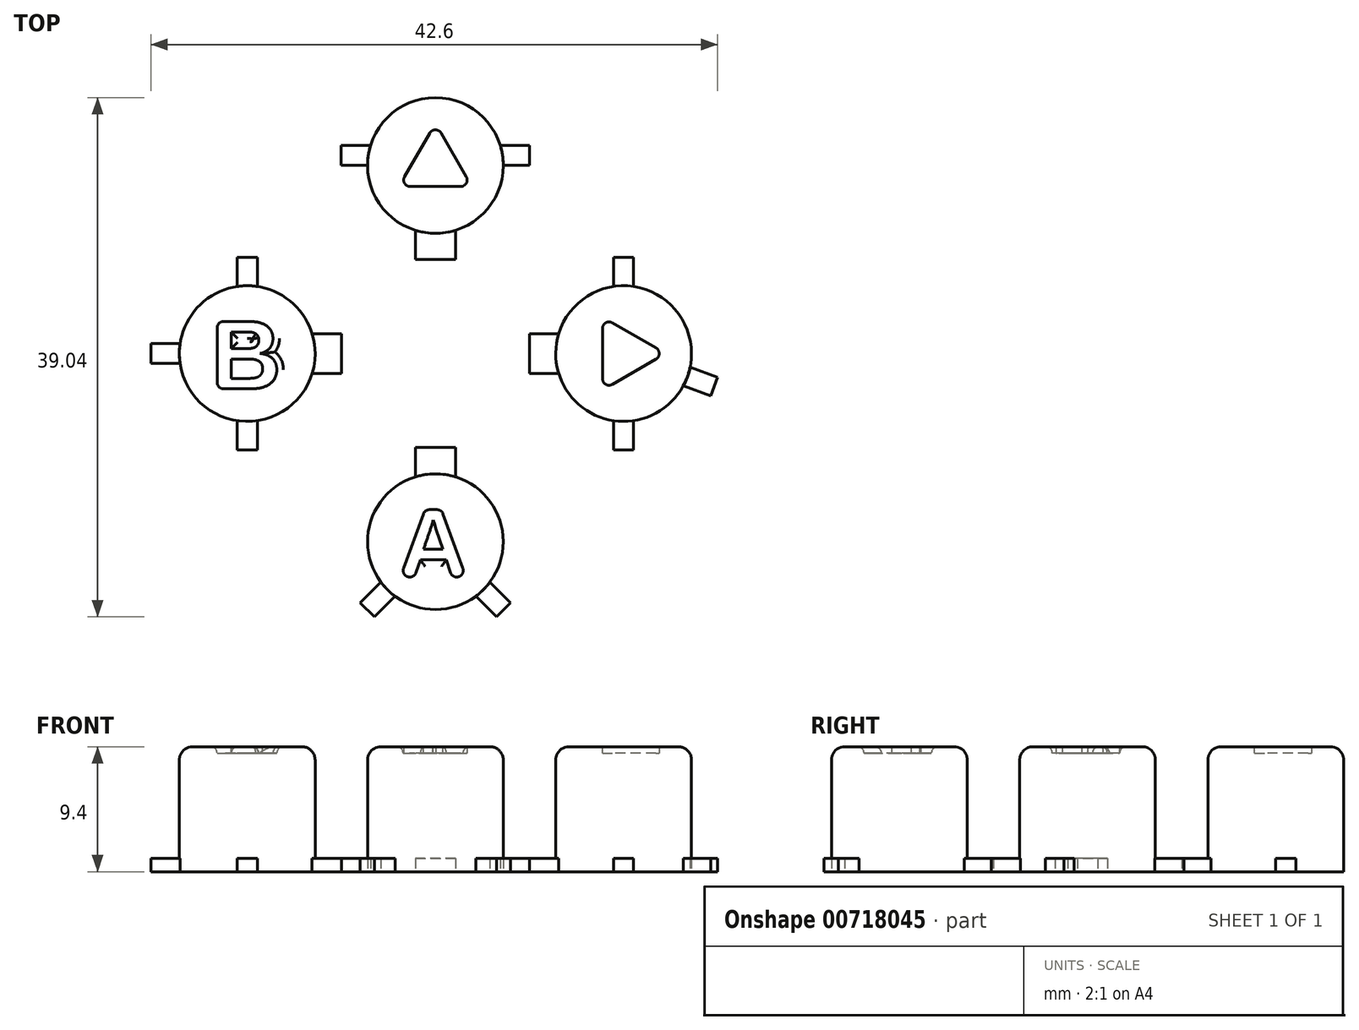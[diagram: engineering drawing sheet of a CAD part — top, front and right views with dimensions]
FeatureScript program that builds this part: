
annotation { "Feature Type Name" : "Feature", "Feature Type Description" : "" }
export const myFeature = defineFeature(function(context is Context, id is Id, definition is map)
    precondition{}
    {
        {
            var Q0;
            Q0=qCreatedBy(makeId("Top.planeOp"),FACE);
            var sketch = newSketch(context, id + "F0", { "sketchPlane" : qUnion([Q0])});
            skCircle(sketch, "E0", {"center": v(0, 14.14) * mm, "radius": 5.1 * mm});
            skLineSegment(sketch, "E1.top", {"start": v(1.5, 7.07) * mm, "end": v(-1.5, 7.07) * mm});
            skLineSegment(sketch, "E1.left", {"start": v(1.5, 9.27) * mm, "end": v(1.5, 7.07) * mm});
            skLineSegment(sketch, "E1.right", {"start": v(-1.5, 9.27) * mm, "end": v(-1.5, 7.07) * mm});
            skLineSegment(sketch, "E2.bottom", {"start": v(-7.07, 15.64) * mm, "end": v(-4.87, 15.64) * mm});
            skLineSegment(sketch, "E2.top", {"start": v(-7.07, 14.14) * mm, "end": v(-5.1, 14.14) * mm});
            skLineSegment(sketch, "E2.left", {"start": v(-7.07, 15.64) * mm, "end": v(-7.07, 14.14) * mm});
            skLineSegment(sketch, "E2.right", {"start": v(7.07, 15.64) * mm, "end": v(7.07, 14.14) * mm});
            skLineSegment(sketch, "E3.trimOffspring", {"start": v(4.87, 15.64) * mm, "end": v(7.07, 15.64) * mm});
            skLineSegment(sketch, "E4.trimOffspring", {"start": v(5.1, 14.14) * mm, "end": v(7.07, 14.14) * mm});
            skLineSegment(sketch, "E5.bottom", {"start": v(-14.14, 0) * mm, "end": v(0, 14.14) * mm, "construction": true});
            skLineSegment(sketch, "E5.top", {"start": v(0, -14.14) * mm, "end": v(14.14, 0) * mm, "construction": true});
            skLineSegment(sketch, "E5.left", {"start": v(-14.14, 0) * mm, "end": v(0, -14.14) * mm, "construction": true});
            skLineSegment(sketch, "E5.right", {"start": v(0, 14.14) * mm, "end": v(14.14, 0) * mm, "construction": true});
            skPoint(sketch, "E5.middle", {"position": v(0, 0) * mm});
            skCircle(sketch, "E6", {"center": v(14.14, 0) * mm, "radius": 5.1 * mm});
            skCircle(sketch, "E7", {"center": v(0, -14.14) * mm, "radius": 5.1 * mm});
            skLineSegment(sketch, "E8", {"start": v(0, 14.14) * mm, "end": v(0, 0) * mm, "construction": true});
            skLineSegment(sketch, "E9.bottom", {"start": v(-1.5, -7.07) * mm, "end": v(1.5, -7.07) * mm});
            skLineSegment(sketch, "E9.left", {"start": v(-1.5, -7.07) * mm, "end": v(-1.5, -9.27) * mm});
            skLineSegment(sketch, "E9.right", {"start": v(1.5, -7.07) * mm, "end": v(1.5, -9.27) * mm});
            skLineSegment(sketch, "E10.bottom", {"start": v(7.07, 1.5) * mm, "end": v(9.27, 1.5) * mm});
            skLineSegment(sketch, "E10.top", {"start": v(7.07, -1.5) * mm, "end": v(9.27, -1.5) * mm});
            skLineSegment(sketch, "E10.left", {"start": v(7.07, 1.5) * mm, "end": v(7.07, -1.5) * mm});
            skLineSegment(sketch, "E11", {"start": v(13.4, 5.04) * mm, "end": v(13.4, 7.24) * mm});
            skLineSegment(sketch, "E12", {"start": v(13.4, 7.24) * mm, "end": v(14.9, 7.24) * mm});
            skLineSegment(sketch, "E13", {"start": v(14.9, 7.24) * mm, "end": v(14.9, 5.04) * mm});
            skLineSegment(sketch, "E14", {"start": v(13.4, -5.04) * mm, "end": v(13.4, -7.24) * mm});
            skLineSegment(sketch, "E15", {"start": v(13.4, -7.24) * mm, "end": v(14.9, -7.24) * mm});
            skLineSegment(sketch, "E16", {"start": v(14.9, -7.24) * mm, "end": v(14.9, -5.04) * mm});
            skLineSegment(sketch, "E17.top", {"start": v(20.7, -3.18) * mm, "end": v(21.2, -1.77) * mm});
            skLineSegment(sketch, "E17.left", {"start": v(18.63, -2.43) * mm, "end": v(20.7, -3.18) * mm});
            skLineSegment(sketch, "E17.right", {"start": v(19.14, -1.02) * mm, "end": v(21.2, -1.77) * mm});
            skLineSegment(sketch, "E18", {"start": v(14.14, 0) * mm, "end": v(20.95, -2.48) * mm, "construction": true});
            skCircle(sketch, "E19", {"center": v(-14.14, 0) * mm, "radius": 5.1 * mm});
            skLineSegment(sketch, "E20.bottom", {"start": v(-9.27, 1.5) * mm, "end": v(-7.07, 1.5) * mm});
            skLineSegment(sketch, "E20.top", {"start": v(-9.27, -1.5) * mm, "end": v(-7.07, -1.5) * mm});
            skLineSegment(sketch, "E20.right", {"start": v(-7.07, 1.5) * mm, "end": v(-7.07, -1.5) * mm});
            skLineSegment(sketch, "E21.bottom", {"start": v(-14.9, 7.24) * mm, "end": v(-13.4, 7.24) * mm});
            skLineSegment(sketch, "E21.top", {"start": v(-14.9, -7.24) * mm, "end": v(-13.4, -7.24) * mm});
            skLineSegment(sketch, "E21.left", {"start": v(-14.9, 7.24) * mm, "end": v(-14.9, 5.04) * mm});
            skLineSegment(sketch, "E21.right", {"start": v(-13.4, 7.24) * mm, "end": v(-13.4, 5.04) * mm});
            skLineSegment(sketch, "E22.bottom", {"start": v(-21.39, 0.75) * mm, "end": v(-19.19, 0.75) * mm});
            skLineSegment(sketch, "E22.top", {"start": v(-21.39, -0.75) * mm, "end": v(-19.19, -0.75) * mm});
            skLineSegment(sketch, "E22.left", {"start": v(-21.39, 0.75) * mm, "end": v(-21.39, -0.75) * mm});
            skLineSegment(sketch, "E23.trimOffspring", {"start": v(-14.9, -5.04) * mm, "end": v(-14.9, -7.24) * mm});
            skLineSegment(sketch, "E24.trimOffspring", {"start": v(-13.4, -5.04) * mm, "end": v(-13.4, -7.24) * mm});
            skLineSegment(sketch, "E25", {"start": v(0, -14.14) * mm, "end": v(5.12, -19.26) * mm, "construction": true});
            skLineSegment(sketch, "E26", {"start": v(0, -14.14) * mm, "end": v(-5.12, -19.26) * mm, "construction": true});
            skLineSegment(sketch, "E27.top", {"start": v(-5.65, -18.73) * mm, "end": v(-4.6, -19.8) * mm});
            skLineSegment(sketch, "E27.left", {"start": v(-4.1, -17.18) * mm, "end": v(-5.65, -18.73) * mm});
            skLineSegment(sketch, "E27.right", {"start": v(-3.04, -18.24) * mm, "end": v(-4.6, -19.8) * mm});
            skLineSegment(sketch, "E28", {"start": v(3.04, -18.24) * mm, "end": v(4.6, -19.8) * mm});
            skLineSegment(sketch, "E29", {"start": v(4.6, -19.8) * mm, "end": v(5.65, -18.73) * mm});
            skLineSegment(sketch, "E30", {"start": v(5.65, -18.73) * mm, "end": v(4.1, -17.18) * mm});
            skSolve(sketch);
        }
        {
            var Q0;
            {var subQ0=sQuery(id+"F0.wireOp",EDGE,"E0");var subQ4=makeQuery(id+"F0.imprint","INTERSECT",VERTEX,{"derivedFrom":[subQ0,sQuery(id+"F0.wireOp",EDGE,"E3.trimOffspring")]});Q0=makeQuery(id+"F0.imprint","IMPRINT",FACE,{"disambiguationData":[TD([[makeQuery(id+"F0.imprint","IMPRINT",EDGE,{"disambiguationData":[TD([[subQ4,1.0]])],"derivedFrom":subQ0}),1.0]])]});}
            var Q1;
            {var subQ0=sQuery(id+"F0.wireOp",EDGE,"E19");var subQ5=makeQuery(id+"F0.imprint","INTERSECT",VERTEX,{"derivedFrom":[subQ0,sQuery(id+"F0.wireOp",EDGE,"E20.bottom")]});Q1=makeQuery(id+"F0.imprint","IMPRINT",FACE,{"disambiguationData":[TD([[makeQuery(id+"F0.imprint","IMPRINT",EDGE,{"disambiguationData":[TD([[subQ5,-1.0]])],"derivedFrom":subQ0}),1.0]])]});}
            var Q2;
            {var subQ0=sQuery(id+"F0.wireOp",EDGE,"E6");var subQ4=makeQuery(id+"F0.imprint","INTERSECT",VERTEX,{"derivedFrom":[subQ0,sQuery(id+"F0.wireOp",EDGE,"E11")]});Q2=makeQuery(id+"F0.imprint","IMPRINT",FACE,{"disambiguationData":[TD([[makeQuery(id+"F0.imprint","IMPRINT",EDGE,{"disambiguationData":[TD([[subQ4,1.0]])],"derivedFrom":subQ0}),1.0]])]});}
            var Q3;
            {var subQ0=sQuery(id+"F0.wireOp",EDGE,"E7");var subQ4=makeQuery(id+"F0.imprint","INTERSECT",VERTEX,{"derivedFrom":[subQ0,sQuery(id+"F0.wireOp",EDGE,"E9.left")]});Q3=makeQuery(id+"F0.imprint","IMPRINT",FACE,{"disambiguationData":[TD([[makeQuery(id+"F0.imprint","IMPRINT",EDGE,{"disambiguationData":[TD([[subQ4,1.0]])],"derivedFrom":subQ0}),1.0]])]});}
            extrude(context, id + "F1", {"entities" : qUnion([Q0, Q1, Q2, Q3]), "depth" : 9.4 * mm, "offsetDistance" : 25 * mm});
        }
        {
            var Q0;
            {var subQ0=sQuery(id+"F0.wireOp",EDGE,"E2.bottom");Q0=makeQuery(id+"F0.imprint","IMPRINT",FACE,{"disambiguationData":[TD([[makeQuery(id+"F0.imprint","IMPRINT",EDGE,{"derivedFrom":subQ0}),-1.0]])]});}
            var Q1;
            Q1=makeQuery(id+"F0.imprint","IMPRINT",FACE,{"disambiguationData":[TD([[makeQuery(id+"F0.imprint","IMPRINT",EDGE,{"derivedFrom":sQuery(id+"F0.wireOp",EDGE,"E2.right")}),-1.0]])]});
            var Q2;
            Q2=makeQuery(id+"F0.imprint","IMPRINT",FACE,{"disambiguationData":[TD([[makeQuery(id+"F0.imprint","IMPRINT",EDGE,{"derivedFrom":sQuery(id+"F0.wireOp",EDGE,"E1.top")}),-1.0]])]});
            var Q3;
            {var subQ0=sQuery(id+"F0.wireOp",EDGE,"E22.bottom");Q3=makeQuery(id+"F0.imprint","IMPRINT",FACE,{"disambiguationData":[TD([[makeQuery(id+"F0.imprint","IMPRINT",EDGE,{"derivedFrom":subQ0}),-1.0]])]});}
            var Q4;
            Q4=makeQuery(id+"F0.imprint","IMPRINT",FACE,{"disambiguationData":[TD([[makeQuery(id+"F0.imprint","IMPRINT",EDGE,{"derivedFrom":sQuery(id+"F0.wireOp",EDGE,"E21.top")}),1.0]])]});
            var Q5;
            Q5=makeQuery(id+"F0.imprint","IMPRINT",FACE,{"disambiguationData":[TD([[makeQuery(id+"F0.imprint","IMPRINT",EDGE,{"derivedFrom":sQuery(id+"F0.wireOp",EDGE,"E21.bottom")}),-1.0]])]});
            var Q6;
            {var subQ0=sQuery(id+"F0.wireOp",EDGE,"E20.bottom");Q6=makeQuery(id+"F0.imprint","IMPRINT",FACE,{"disambiguationData":[TD([[makeQuery(id+"F0.imprint","IMPRINT",EDGE,{"derivedFrom":subQ0}),-1.0]])]});}
            var Q7;
            {var subQ0=sQuery(id+"F0.wireOp",EDGE,"E10.bottom");Q7=makeQuery(id+"F0.imprint","IMPRINT",FACE,{"disambiguationData":[TD([[makeQuery(id+"F0.imprint","IMPRINT",EDGE,{"derivedFrom":subQ0}),-1.0]])]});}
            var Q8;
            {var subQ0=sQuery(id+"F0.wireOp",EDGE,"E11");Q8=makeQuery(id+"F0.imprint","IMPRINT",FACE,{"disambiguationData":[TD([[makeQuery(id+"F0.imprint","IMPRINT",EDGE,{"derivedFrom":subQ0}),-1.0]])]});}
            var Q9;
            {var subQ0=sQuery(id+"F0.wireOp",EDGE,"E14");Q9=makeQuery(id+"F0.imprint","IMPRINT",FACE,{"disambiguationData":[TD([[makeQuery(id+"F0.imprint","IMPRINT",EDGE,{"derivedFrom":subQ0}),1.0]])]});}
            var Q10;
            Q10=makeQuery(id+"F0.imprint","IMPRINT",FACE,{"disambiguationData":[TD([[makeQuery(id+"F0.imprint","IMPRINT",EDGE,{"derivedFrom":sQuery(id+"F0.wireOp",EDGE,"E17.top")}),1.0]])]});
            var Q11;
            Q11=makeQuery(id+"F0.imprint","IMPRINT",FACE,{"disambiguationData":[TD([[makeQuery(id+"F0.imprint","IMPRINT",EDGE,{"derivedFrom":sQuery(id+"F0.wireOp",EDGE,"E9.bottom")}),-1.0]])]});
            var Q12;
            Q12=makeQuery(id+"F0.imprint","IMPRINT",FACE,{"disambiguationData":[TD([[makeQuery(id+"F0.imprint","IMPRINT",EDGE,{"derivedFrom":sQuery(id+"F0.wireOp",EDGE,"E27.top")}),1.0]])]});
            var Q13;
            {var subQ0=sQuery(id+"F0.wireOp",EDGE,"E28");Q13=makeQuery(id+"F0.imprint","IMPRINT",FACE,{"disambiguationData":[TD([[makeQuery(id+"F0.imprint","IMPRINT",EDGE,{"derivedFrom":subQ0}),1.0]])]});}
            extrude(context, id + "F2", {"entities" : qUnion([Q0, Q1, Q2, Q3, Q4, Q5, Q6, Q7, Q8, Q9, Q10, Q11, Q12, Q13]), "operationType" : NewBodyOperationType.ADD, "depth" : 1 * mm, "offsetDistance" : 25 * mm});
        }
        {
            var Q0;
            Q0=makeQuery(id+"F1.opExtrude","CAP_FACE",FACE,{"disambiguationData":[OSD([sQuery(id+"F0.wireOp",EDGE,"E0")])],"isStart":false});
            var sketch = newSketch(context, id + "F3", { "sketchPlane" : qUnion([Q0])});
            skCircle(sketch, "E31.cCircle", {"center": v(0, 14.14) * mm, "radius": 1.59 * mm, "construction": true});
            skLineSegment(sketch, "E31.0", {"start": v(2.75, 12.55) * mm, "end": v(-2.75, 12.55) * mm});
            skLineSegment(sketch, "E31.1", {"start": v(-2.75, 12.55) * mm, "end": v(0, 17.32) * mm});
            skLineSegment(sketch, "E31.2", {"start": v(0, 17.32) * mm, "end": v(2.75, 12.55) * mm});
            skCircle(sketch, "E32.cCircle", {"center": v(14.14, 0) * mm, "radius": 1.59 * mm, "construction": true});
            skLineSegment(sketch, "E32.0", {"start": v(17.32, 0) * mm, "end": v(12.55, -2.75) * mm});
            skLineSegment(sketch, "E32.1", {"start": v(12.55, -2.75) * mm, "end": v(12.55, 2.75) * mm});
            skLineSegment(sketch, "E32.2", {"start": v(12.55, 2.75) * mm, "end": v(17.32, 0) * mm});
            skText(sketch, "E33", { "text": "A", "fontName": "Arimo-Bold.ttf"});
            skText(sketch, "E34", { "text": "B", "fontName": "Arimo-Bold.ttf"});
            skPoint(sketch, "E35", {"position": v(-14.14, 0) * mm});
            skPoint(sketch, "E36", {"position": v(0, -14.14) * mm});
            const initialGuessF3  = {"E33": [-0.00282, -0.0168, 1, 0, 0.0053], "E34": [-0.0169, -0.00265, 1, 0, 0.0053]};
            skSetInitialGuess(sketch, initialGuessF3);
            skSolve(sketch);
        }
        {
            var Q0;
            Q0=makeQuery(id+"F3.imprint","IMPRINT",FACE,{"disambiguationData":[TD([[makeQuery(id+"F3.imprint","IMPRINT",EDGE,{"derivedFrom":sQuery(id+"F3.wireOp",EDGE,"E33.sketch_text.stroke-0")}),-1.0]])]});
            var sketch = newSketch(context, id + "F4", { "sketchPlane" : qUnion([Q0])});
            skLineSegment(sketch, "E37", {"start": v(-0.89, -14.7) * mm, "end": v(-0.16, -12.57) * mm});
            skLineSegment(sketch, "E38", {"start": v(-0.16, -12.57) * mm, "end": v(0.57, -14.7) * mm});
            skLineSegment(sketch, "E39.0.0", {"start": v(0.07, -13.24) * mm, "end": v(-0.08, -12.75) * mm, "construction": true});
            skLineSegment(sketch, "E39.0.1", {"start": v(-0.08, -12.75) * mm, "end": v(-0.16, -12.5) * mm, "construction": true});
            skLineSegment(sketch, "E39.0.2", {"start": v(-0.16, -12.5) * mm, "end": v(-0.18, -12.58) * mm, "construction": true});
            skFitSpline(sketch, "E39.0.3", {"points": [v(-0.18, -12.58) * mm, v(-0.22, -12.71) * mm, v(-0.27, -12.88) * mm], "construction": true});
            skFitSpline(sketch, "E39.0.4", {"points": [v(-0.27, -12.88) * mm, v(-0.32, -13.05) * mm, v(-0.89, -14.7) * mm]});
            skLineSegment(sketch, "E39.0.5", {"start": v(-0.89, -14.7) * mm, "end": v(0.57, -14.7) * mm});
            skLineSegment(sketch, "E39.0.6", {"start": v(0.57, -14.7) * mm, "end": v(0.07, -13.24) * mm});
            skSolve(sketch);
        }
        {
            var Q0;
            Q0=makeQuery(id+"F3.imprint","IMPRINT",FACE,{"disambiguationData":[TD([[makeQuery(id+"F3.imprint","IMPRINT",EDGE,{"derivedFrom":sQuery(id+"F3.wireOp",EDGE,"E31.0")}),-1.0]])]});
            var Q1;
            Q1=makeQuery(id+"F3.imprint","IMPRINT",FACE,{"disambiguationData":[TD([[makeQuery(id+"F3.imprint","IMPRINT",EDGE,{"derivedFrom":sQuery(id+"F3.wireOp",EDGE,"E34.sketch_text.stroke-0")}),-1.0]])]});
            var Q2;
            Q2=makeQuery(id+"F3.imprint","IMPRINT",FACE,{"disambiguationData":[TD([[makeQuery(id+"F3.imprint","IMPRINT",EDGE,{"derivedFrom":sQuery(id+"F3.wireOp",EDGE,"E33.sketch_text.stroke-0")}),-1.0]])]});
            var Q3;
            Q3=makeQuery(id+"F3.imprint","IMPRINT",FACE,{"disambiguationData":[TD([[makeQuery(id+"F3.imprint","IMPRINT",EDGE,{"derivedFrom":sQuery(id+"F3.wireOp",EDGE,"E32.0")}),-1.0]])]});
            var Q4;
            {var subQ1=sQuery(id+"F4.wireOp",EDGE,"E38");Q4=makeQuery(id+"F4.imprint","IMPRINT",FACE,{"disambiguationData":[TD([[makeQuery(id+"F4.imprint","IMPRINT",EDGE,{"derivedFrom":subQ1}),1.0]])]});}
            extrude(context, id + "F5", {"entities" : qUnion([Q0, Q1, Q2, Q3, Q4]), "operationType" : NewBodyOperationType.REMOVE, "oppositeDirection" : true, "depth" : 0.5 * mm, "offsetDistance" : 25 * mm});
        }
        {
            var Q0;
            Q0=makeQuery(id+"F1.opExtrude","CAP_EDGE",EDGE,{"disambiguationData":[OSD([sQuery(id+"F0.wireOp",EDGE,"E0")])],"isStart":false});
            var Q1;
            Q1=makeQuery(id+"F1.opExtrude","CAP_EDGE",EDGE,{"disambiguationData":[OSD([sQuery(id+"F0.wireOp",EDGE,"E19")])],"isStart":false});
            var Q2;
            Q2=makeQuery(id+"F1.opExtrude","CAP_EDGE",EDGE,{"disambiguationData":[OSD([sQuery(id+"F0.wireOp",EDGE,"E7")])],"isStart":false});
            var Q3;
            Q3=makeQuery(id+"F1.opExtrude","CAP_EDGE",EDGE,{"disambiguationData":[OSD([sQuery(id+"F0.wireOp",EDGE,"E6")])],"isStart":false});
            fillet(context, id + "F6", {"entities" : qUnion([Q0, Q1, Q2, Q3]), "radius" : 1 * mm, "tangentPropagation" : true, "allowEdgeOverflow" : false});
        }
        {
            var Q0;
            Q0=makeQuery(id+"F5.boolean.opBoolean","COPY",EDGE,{"derivedFrom":makeQuery(id+"F5.opExtrude","CAP_EDGE",EDGE,{"disambiguationData":[OSD([sQuery(id+"F3.wireOp",EDGE,"E34.sketch_text.stroke-4")])],"isStart":true})});
            var Q1;
            Q1=makeQuery(id+"F5.boolean.opBoolean","COPY",EDGE,{"derivedFrom":makeQuery(id+"F5.opExtrude","CAP_EDGE",EDGE,{"disambiguationData":[OSD([sQuery(id+"F3.wireOp",EDGE,"E34.sketch_text.stroke-2")])],"isStart":true})});
            var Q2;
            Q2=makeQuery(id+"F5.boolean.opBoolean","COPY",EDGE,{"derivedFrom":makeQuery(id+"F5.opExtrude","CAP_EDGE",EDGE,{"disambiguationData":[OSD([sQuery(id+"F3.wireOp",EDGE,"E34.sketch_text.stroke-3")])],"isStart":true})});
            var Q3;
            Q3=makeQuery(id+"F5.boolean.opBoolean","COPY",EDGE,{"derivedFrom":makeQuery(id+"F5.opExtrude","CAP_EDGE",EDGE,{"disambiguationData":[OSD([sQuery(id+"F3.wireOp",EDGE,"E34.sketch_text.stroke-19")])],"isStart":true})});
            var Q4;
            Q4=makeQuery(id+"F5.boolean.opBoolean","COPY",EDGE,{"derivedFrom":makeQuery(id+"F5.opExtrude","CAP_EDGE",EDGE,{"disambiguationData":[OSD([sQuery(id+"F3.wireOp",EDGE,"E34.sketch_text.stroke-20")])],"isStart":true})});
            var Q5;
            Q5=makeQuery(id+"F5.boolean.opBoolean","COPY",EDGE,{"derivedFrom":makeQuery(id+"F5.opExtrude","CAP_EDGE",EDGE,{"disambiguationData":[OSD([sQuery(id+"F3.wireOp",EDGE,"E34.sketch_text.stroke-14")])],"isStart":true})});
            var Q6;
            Q6=makeQuery(id+"F5.boolean.opBoolean","COPY",EDGE,{"derivedFrom":makeQuery(id+"F5.opExtrude","CAP_EDGE",EDGE,{"disambiguationData":[OSD([sQuery(id+"F3.wireOp",EDGE,"E34.sketch_text.stroke-13")])],"isStart":true})});
            var Q7;
            Q7=makeQuery(id+"F5.boolean.opBoolean","COPY",EDGE,{"derivedFrom":makeQuery(id+"F5.opExtrude","SWEPT_EDGE",EDGE,{"disambiguationData":[OSD([sQuery(id+"F3.wireOp",EDGE,"E34.sketch_text.stroke-3"),sQuery(id+"F3.wireOp",EDGE,"E34.sketch_text.stroke-4")])]})});
            var Q8;
            Q8=makeQuery(id+"F5.boolean.opBoolean","COPY",EDGE,{"derivedFrom":makeQuery(id+"F5.opExtrude","SWEPT_EDGE",EDGE,{"disambiguationData":[OSD([sQuery(id+"F3.wireOp",EDGE,"E34.sketch_text.stroke-2"),sQuery(id+"F3.wireOp",EDGE,"E34.sketch_text.stroke-3")])]})});
            fillet(context, id + "F7", {"entities" : qUnion([Q0, Q1, Q2, Q3, Q4, Q5, Q6, Q7, Q8]), "radius" : 0.49 * mm, "tangentPropagation" : true, "allowEdgeOverflow" : false});
        }
        {
            var Q0;
            Q0=makeQuery(id+"F5.boolean.opBoolean","COPY",EDGE,{"derivedFrom":makeQuery(id+"F5.opExtrude","CAP_EDGE",EDGE,{"disambiguationData":[OSD([sQuery(id+"F3.wireOp",EDGE,"E31.1")])],"isStart":true})});
            var Q1;
            Q1=makeQuery(id+"F5.boolean.opBoolean","COPY",EDGE,{"derivedFrom":makeQuery(id+"F5.opExtrude","CAP_EDGE",EDGE,{"disambiguationData":[OSD([sQuery(id+"F3.wireOp",EDGE,"E31.2")])],"isStart":true})});
            var Q2;
            Q2=makeQuery(id+"F5.boolean.opBoolean","COPY",EDGE,{"derivedFrom":makeQuery(id+"F5.opExtrude","CAP_EDGE",EDGE,{"disambiguationData":[OSD([sQuery(id+"F3.wireOp",EDGE,"E31.0")])],"isStart":true})});
            var Q3;
            Q3=makeQuery(id+"F5.boolean.opBoolean","COPY",EDGE,{"derivedFrom":makeQuery(id+"F5.opExtrude","SWEPT_EDGE",EDGE,{"disambiguationData":[OSD([sQuery(id+"F3.wireOp",EDGE,"E31.1"),sQuery(id+"F3.wireOp",EDGE,"E31.2")])]})});
            var Q4;
            Q4=makeQuery(id+"F5.boolean.opBoolean","COPY",EDGE,{"derivedFrom":makeQuery(id+"F5.opExtrude","SWEPT_EDGE",EDGE,{"disambiguationData":[OSD([sQuery(id+"F3.wireOp",EDGE,"E31.0"),sQuery(id+"F3.wireOp",EDGE,"E31.1")])]})});
            var Q5;
            Q5=makeQuery(id+"F5.boolean.opBoolean","COPY",EDGE,{"derivedFrom":makeQuery(id+"F5.opExtrude","SWEPT_EDGE",EDGE,{"disambiguationData":[OSD([sQuery(id+"F3.wireOp",EDGE,"E31.0"),sQuery(id+"F3.wireOp",EDGE,"E31.2")])]})});
            var Q6;
            Q6=makeQuery(id+"F5.boolean.opBoolean","COPY",EDGE,{"derivedFrom":makeQuery(id+"F5.opExtrude","CAP_EDGE",EDGE,{"disambiguationData":[OSD([sQuery(id+"F3.wireOp",EDGE,"E32.0")])],"isStart":true})});
            var Q7;
            Q7=makeQuery(id+"F5.boolean.opBoolean","COPY",EDGE,{"derivedFrom":makeQuery(id+"F5.opExtrude","CAP_EDGE",EDGE,{"disambiguationData":[OSD([sQuery(id+"F3.wireOp",EDGE,"E32.2")])],"isStart":true})});
            var Q8;
            Q8=makeQuery(id+"F5.boolean.opBoolean","COPY",EDGE,{"derivedFrom":makeQuery(id+"F5.opExtrude","SWEPT_EDGE",EDGE,{"disambiguationData":[OSD([sQuery(id+"F3.wireOp",EDGE,"E32.0"),sQuery(id+"F3.wireOp",EDGE,"E32.2")])]})});
            var Q9;
            Q9=makeQuery(id+"F5.boolean.opBoolean","COPY",EDGE,{"derivedFrom":makeQuery(id+"F5.opExtrude","CAP_EDGE",EDGE,{"disambiguationData":[OSD([sQuery(id+"F3.wireOp",EDGE,"E32.1")])],"isStart":true})});
            var Q10;
            Q10=makeQuery(id+"F5.boolean.opBoolean","COPY",EDGE,{"derivedFrom":makeQuery(id+"F5.opExtrude","SWEPT_EDGE",EDGE,{"disambiguationData":[OSD([sQuery(id+"F3.wireOp",EDGE,"E32.1"),sQuery(id+"F3.wireOp",EDGE,"E32.2")])]})});
            var Q11;
            Q11=makeQuery(id+"F5.boolean.opBoolean","COPY",EDGE,{"derivedFrom":makeQuery(id+"F5.opExtrude","SWEPT_EDGE",EDGE,{"disambiguationData":[OSD([sQuery(id+"F3.wireOp",EDGE,"E32.0"),sQuery(id+"F3.wireOp",EDGE,"E32.1")])]})});
            fillet(context, id + "F8", {"entities" : qUnion([Q0, Q1, Q2, Q3, Q4, Q5, Q6, Q7, Q8, Q9, Q10, Q11]), "radius" : .5 * mm, "tangentPropagation" : true, "allowEdgeOverflow" : false});
        }
        {
            var Q0;
            Q0=makeQuery(id+"F5.boolean.opBoolean","COPY",EDGE,{"derivedFrom":makeQuery(id+"F5.opExtrude","CAP_EDGE",EDGE,{"disambiguationData":[OSD([sQuery(id+"F3.wireOp",EDGE,"E33.sketch_text.stroke-5")])],"isStart":true})});
            var Q1;
            Q1=makeQuery(id+"F5.boolean.opBoolean","COPY",EDGE,{"derivedFrom":makeQuery(id+"F5.opExtrude","CAP_EDGE",EDGE,{"disambiguationData":[OSD([sQuery(id+"F3.wireOp",EDGE,"E33.sketch_text.stroke-6")])],"isStart":true})});
            var Q2;
            Q2=makeQuery(id+"F5.boolean.opBoolean","COPY",EDGE,{"derivedFrom":makeQuery(id+"F5.opExtrude","CAP_EDGE",EDGE,{"disambiguationData":[OSD([sQuery(id+"F3.wireOp",EDGE,"E33.sketch_text.stroke-4")])],"isStart":true})});
            var Q3;
            Q3=makeQuery(id+"F5.boolean.opBoolean","COPY",EDGE,{"derivedFrom":makeQuery(id+"F5.opExtrude","CAP_EDGE",EDGE,{"disambiguationData":[OSD([sQuery(id+"F3.wireOp",EDGE,"E33.sketch_text.stroke-7")])],"isStart":true})});
            var Q4;
            Q4=makeQuery(id+"F5.boolean.opBoolean","COPY",EDGE,{"derivedFrom":makeQuery(id+"F5.opExtrude","CAP_EDGE",EDGE,{"disambiguationData":[OSD([sQuery(id+"F3.wireOp",EDGE,"E33.sketch_text.stroke-3")])],"isStart":true})});
            var Q5;
            Q5=makeQuery(id+"F5.boolean.opBoolean","COPY",EDGE,{"derivedFrom":makeQuery(id+"F5.opExtrude","CAP_EDGE",EDGE,{"disambiguationData":[OSD([sQuery(id+"F3.wireOp",EDGE,"E33.sketch_text.stroke-2")])],"isStart":true})});
            var Q6;
            Q6=makeQuery(id+"F5.boolean.opBoolean","COPY",EDGE,{"derivedFrom":makeQuery(id+"F5.opExtrude","CAP_EDGE",EDGE,{"disambiguationData":[OSD([sQuery(id+"F3.wireOp",EDGE,"E33.sketch_text.stroke-0")])],"isStart":true})});
            var Q7;
            Q7=makeQuery(id+"F5.boolean.opBoolean","COPY",EDGE,{"derivedFrom":makeQuery(id+"F5.opExtrude","CAP_EDGE",EDGE,{"disambiguationData":[OSD([sQuery(id+"F3.wireOp",EDGE,"E33.sketch_text.stroke-1")])],"isStart":true})});
            var Q8;
            Q8=makeQuery(id+"F5.boolean.opBoolean","COPY",EDGE,{"derivedFrom":makeQuery(id+"F5.opExtrude","SWEPT_EDGE",EDGE,{"disambiguationData":[OSD([sQuery(id+"F3.wireOp",EDGE,"E33.sketch_text.stroke-3"),sQuery(id+"F3.wireOp",EDGE,"E33.sketch_text.stroke-4")])]})});
            var Q9;
            Q9=makeQuery(id+"F5.boolean.opBoolean","COPY",EDGE,{"derivedFrom":makeQuery(id+"F5.opExtrude","SWEPT_EDGE",EDGE,{"disambiguationData":[OSD([sQuery(id+"F3.wireOp",EDGE,"E33.sketch_text.stroke-6"),sQuery(id+"F3.wireOp",EDGE,"E33.sketch_text.stroke-7")])]})});
            var Q10;
            Q10=makeQuery(id+"F5.boolean.opBoolean","COPY",EDGE,{"derivedFrom":makeQuery(id+"F5.opExtrude","SWEPT_EDGE",EDGE,{"disambiguationData":[OSD([sQuery(id+"F3.wireOp",EDGE,"E33.sketch_text.stroke-2"),sQuery(id+"F3.wireOp",EDGE,"E33.sketch_text.stroke-3")])]})});
            var Q11;
            Q11=makeQuery(id+"F5.boolean.opBoolean","COPY",EDGE,{"derivedFrom":makeQuery(id+"F5.opExtrude","SWEPT_EDGE",EDGE,{"disambiguationData":[OSD([sQuery(id+"F3.wireOp",EDGE,"E33.sketch_text.stroke-0"),sQuery(id+"F3.wireOp",EDGE,"E33.sketch_text.stroke-7")])]})});
            var Q12;
            Q12=makeQuery(id+"F5.boolean.opBoolean","COPY",EDGE,{"derivedFrom":makeQuery(id+"F5.opExtrude","SWEPT_EDGE",EDGE,{"disambiguationData":[OSD([sQuery(id+"F3.wireOp",EDGE,"E33.sketch_text.stroke-4"),sQuery(id+"F3.wireOp",EDGE,"E33.sketch_text.stroke-5")])]})});
            var Q13;
            Q13=makeQuery(id+"F5.boolean.opBoolean","COPY",EDGE,{"derivedFrom":makeQuery(id+"F5.opExtrude","SWEPT_EDGE",EDGE,{"disambiguationData":[OSD([sQuery(id+"F3.wireOp",EDGE,"E33.sketch_text.stroke-5"),sQuery(id+"F3.wireOp",EDGE,"E33.sketch_text.stroke-6")])]})});
            var Q14;
            Q14=makeQuery(id+"F5.boolean.opBoolean","COPY",EDGE,{"derivedFrom":makeQuery(id+"F5.opExtrude","CAP_EDGE",EDGE,{"disambiguationData":[OSD([sQuery(id+"F3.wireOp",EDGE,"E33.sketch_text.stroke-10")])],"isStart":true})});
            var Q15;
            Q15=makeQuery(id+"F5.boolean.opBoolean","TWEAK_EDGE",EDGE,{"derivedFrom":[makeQuery(id+"F5.opExtrude","CAP_EDGE",EDGE,{"disambiguationData":[OSD([sQuery(id+"F3.wireOp",EDGE,"E33.sketch_text.stroke-12")])],"isStart":true}),makeQuery(id+"F5.opExtrude","CAP_EDGE",EDGE,{"disambiguationData":[OSD([sQuery(id+"F4.wireOp",EDGE,"E38")])],"isStart":true})]});
            var Q16;
            Q16=makeQuery(id+"F5.boolean.opBoolean","COPY",EDGE,{"derivedFrom":makeQuery(id+"F5.opExtrude","CAP_EDGE",EDGE,{"disambiguationData":[OSD([sQuery(id+"F3.wireOp",EDGE,"E33.sketch_text.stroke-11")])],"isStart":true})});
            var Q17;
            Q17=makeQuery(id+"F5.boolean.opBoolean","COPY",EDGE,{"derivedFrom":makeQuery(id+"F5.opExtrude","CAP_EDGE",EDGE,{"disambiguationData":[OSD([sQuery(id+"F4.wireOp",EDGE,"E37")])],"isStart":true})});
            fillet(context, id + "F9", {"entities" : qUnion([Q0, Q1, Q2, Q3, Q4, Q5, Q6, Q7, Q8, Q9, Q10, Q11, Q12, Q13, Q14, Q15, Q16, Q17]), "radius" : 0.49 * mm, "tangentPropagation" : true, "allowEdgeOverflow" : false});
        }
    });
